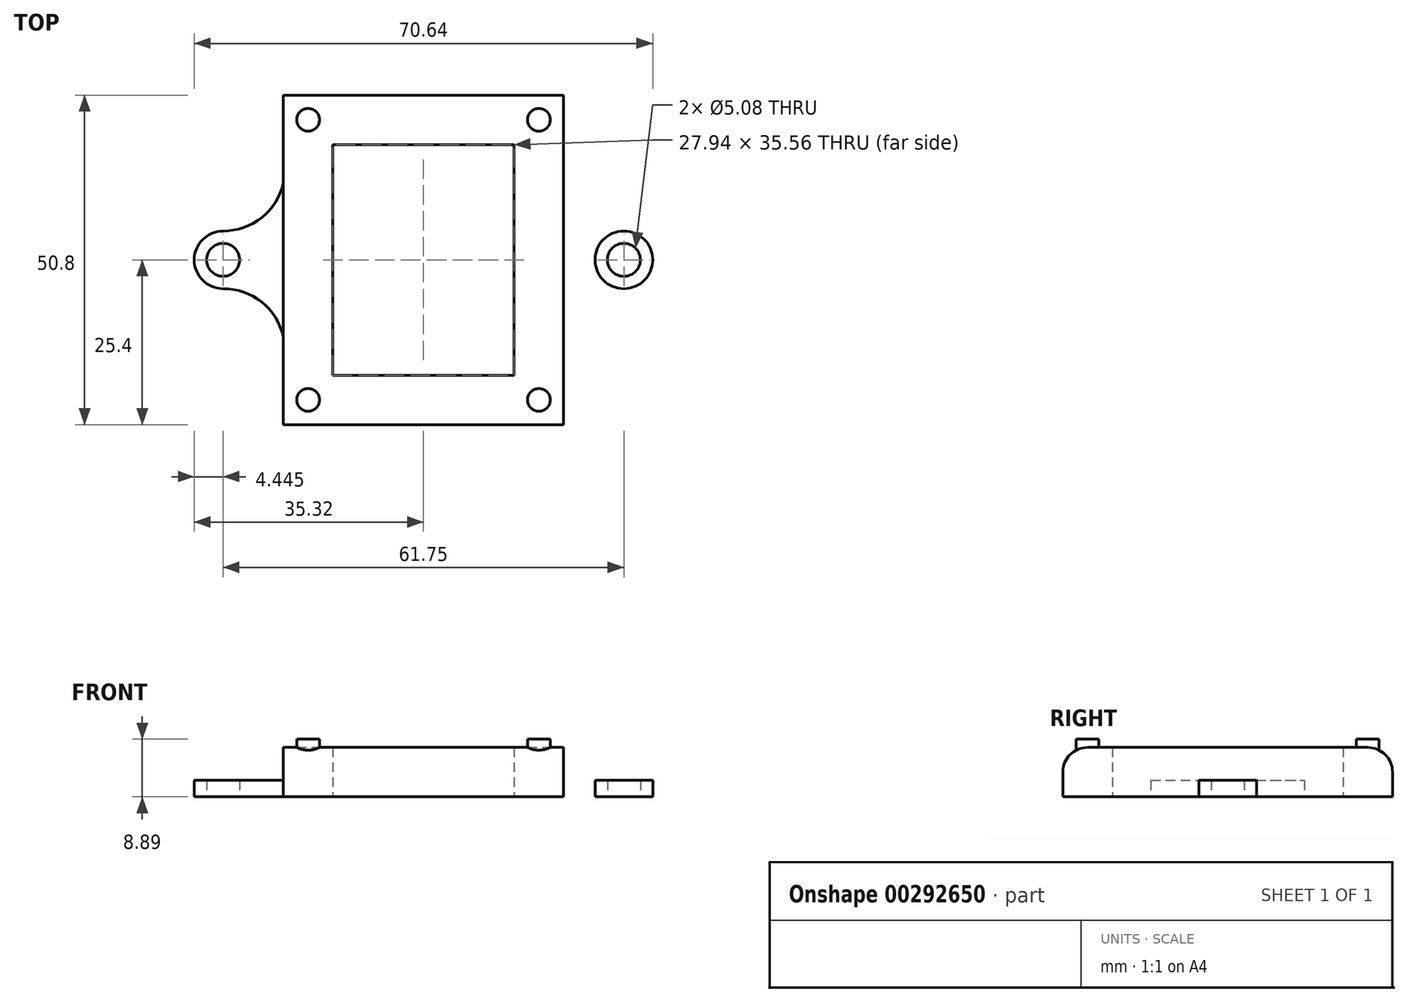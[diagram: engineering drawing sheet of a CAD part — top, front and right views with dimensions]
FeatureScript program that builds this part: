
annotation { "Feature Type Name" : "Feature", "Feature Type Description" : "" }
export const myFeature = defineFeature(function(context is Context, id is Id, definition is map)
    precondition{}
    {
        {
            var Q0;
            Q0=qCreatedBy(makeId("Top.planeOp"),FACE);
            var sketch = newSketch(context, id + "F0", { "sketchPlane" : qUnion([Q0])});
            skLineSegment(sketch, "E0.bottom", {"start": v(21.59, -25.4) * mm, "end": v(-21.59, -25.4) * mm});
            skLineSegment(sketch, "E0.top", {"start": v(21.59, 25.4) * mm, "end": v(-21.59, 25.4) * mm});
            skLineSegment(sketch, "E0.left", {"start": v(21.59, -25.4) * mm, "end": v(21.59, 25.4) * mm});
            skLineSegment(sketch, "E0.right", {"start": v(-21.59, -25.4) * mm, "end": v(-21.59, 25.4) * mm});
            skPoint(sketch, "E0.middle", {"position": v(0, 0) * mm});
            skCircle(sketch, "E1", {"center": v(-17.78, 21.59) * mm, "radius": 1.75 * mm});
            skCircle(sketch, "E2", {"center": v(17.78, 21.59) * mm, "radius": 1.75 * mm});
            skCircle(sketch, "E3", {"center": v(-17.78, -21.6) * mm, "radius": 1.75 * mm});
            skCircle(sketch, "E4", {"center": v(17.78, -21.6) * mm, "radius": 1.75 * mm});
            skLineSegment(sketch, "E5.bottom", {"start": v(13.97, -17.78) * mm, "end": v(-13.97, -17.78) * mm});
            skLineSegment(sketch, "E5.top", {"start": v(13.97, 17.78) * mm, "end": v(-13.97, 17.78) * mm});
            skLineSegment(sketch, "E5.left", {"start": v(13.97, -17.78) * mm, "end": v(13.97, 17.78) * mm});
            skLineSegment(sketch, "E5.right", {"start": v(-13.97, -17.78) * mm, "end": v(-13.97, 17.78) * mm});
            skCircle(sketch, "E6", {"center": v(30.88, 0) * mm, "radius": 2.54 * mm});
            skPoint(sketch, "E6.centerSnap0", {"position": v(21.59, 0) * mm});
            skCircle(sketch, "E7", {"center": v(-30.88, 0) * mm, "radius": 2.54 * mm});
            skPoint(sketch, "E7.centerSnap0", {"position": v(-21.59, 0) * mm});
            skCircle(sketch, "E8", {"center": v(-30.88, 0) * mm, "radius": 4.45 * mm});
            skCircle(sketch, "E9", {"center": v(30.88, 0) * mm, "radius": 4.45 * mm});
            skArc(sketch, "E10", {"start": v(30.88, 4.45) * mm, "mid": v(24.94, 6.52) * mm, "end": v(21.59, 11.85) * mm});
            skArc(sketch, "E11", {"start": v(30.88, -4.45) * mm, "mid": v(24.94, -6.52) * mm, "end": v(21.59, -11.85) * mm});
            skArc(sketch, "E12", {"start": v(-30.87, 4.45) * mm, "mid": v(-24.94, 6.52) * mm, "end": v(-21.59, 11.85) * mm});
            skArc(sketch, "E13", {"start": v(-30.87, -4.45) * mm, "mid": v(-24.94, -6.52) * mm, "end": v(-21.59, -11.85) * mm});
            skSolve(sketch);
        }
        {
            var Q0;
            {var subQ0=sQuery(id+"F0.wireOp",EDGE,"E12");Q0=makeQuery(id+"F0.imprint","IMPRINT",FACE,{"disambiguationData":[TD([[makeQuery(id+"F0.imprint","IMPRINT",EDGE,{"derivedFrom":subQ0}),-1.0]])]});}
            var Q1;
            Q1=makeQuery(id+"F0.imprint","IMPRINT",FACE,{"disambiguationData":[TD([[makeQuery(id+"F0.imprint","IMPRINT",EDGE,{"derivedFrom":sQuery(id+"F0.wireOp",EDGE,"E7")}),-1.0]])]});
            var Q2;
            {var subQ0=sQuery(id+"F0.wireOp",EDGE,"E10");Q2=makeQuery(id+"F0.imprint","IMPRINT",FACE,{"disambiguationData":[TD([[makeQuery(id+"F0.imprint","IMPRINT",EDGE,{"derivedFrom":subQ0}),1.0]])]});}
            var Q3;
            Q3=makeQuery(id+"F0.imprint","IMPRINT",FACE,{"disambiguationData":[TD([[makeQuery(id+"F0.imprint","IMPRINT",EDGE,{"derivedFrom":sQuery(id+"F0.wireOp",EDGE,"E6")}),-1.0]])]});
            extrude(context, id + "F1", {"entities" : qUnion([Q0, Q1, Q2, Q3]), "depth" : 2.54 * mm});
        }
        {
            var Q0;
            {var subQ4=sQuery(id+"F0.wireOp",EDGE,"E0.bottom");Q0=makeQuery(id+"F0.imprint","IMPRINT",FACE,{"disambiguationData":[TD([[makeQuery(id+"F0.imprint","IMPRINT",EDGE,{"derivedFrom":subQ4}),-1.0]])]});}
            extrude(context, id + "F2", {"entities" : qUnion([Q0]), "depth" : 7.62 * mm});
        }
        {
            var Q0;
            Q0=makeQuery(id+"F0.imprint","IMPRINT",FACE,{"disambiguationData":[TD([[makeQuery(id+"F0.imprint","IMPRINT",EDGE,{"derivedFrom":sQuery(id+"F0.wireOp",EDGE,"E1")}),1.0]])]});
            var Q1;
            Q1=makeQuery(id+"F0.imprint","IMPRINT",FACE,{"disambiguationData":[TD([[makeQuery(id+"F0.imprint","IMPRINT",EDGE,{"derivedFrom":sQuery(id+"F0.wireOp",EDGE,"E3")}),1.0]])]});
            var Q2;
            Q2=makeQuery(id+"F0.imprint","IMPRINT",FACE,{"disambiguationData":[TD([[makeQuery(id+"F0.imprint","IMPRINT",EDGE,{"derivedFrom":sQuery(id+"F0.wireOp",EDGE,"E4")}),1.0]])]});
            var Q3;
            Q3=makeQuery(id+"F0.imprint","IMPRINT",FACE,{"disambiguationData":[TD([[makeQuery(id+"F0.imprint","IMPRINT",EDGE,{"derivedFrom":sQuery(id+"F0.wireOp",EDGE,"E2")}),1.0]])]});
            extrude(context, id + "F3", {"entities" : qUnion([Q0, Q1, Q2, Q3]), "operationType" : NewBodyOperationType.ADD, "depth" : 8.9 * mm});
        }
        {
            var Q0;
            Q0=makeQuery(id+"F2.opExtrude","CAP_EDGE",EDGE,{"disambiguationData":[OSD([sQuery(id+"F0.wireOp",EDGE,"E0.bottom")])],"isStart":false});
            var Q1;
            Q1=makeQuery(id+"F2.opExtrude","CAP_EDGE",EDGE,{"disambiguationData":[OSD([sQuery(id+"F0.wireOp",EDGE,"E0.top")])],"isStart":false});
            fillet(context, id + "F4", {"entities" : qUnion([Q0, Q1]), "radius" : 3.8 * mm, "tangentPropagation" : true, "allowEdgeOverflow" : false});
        }
    });
